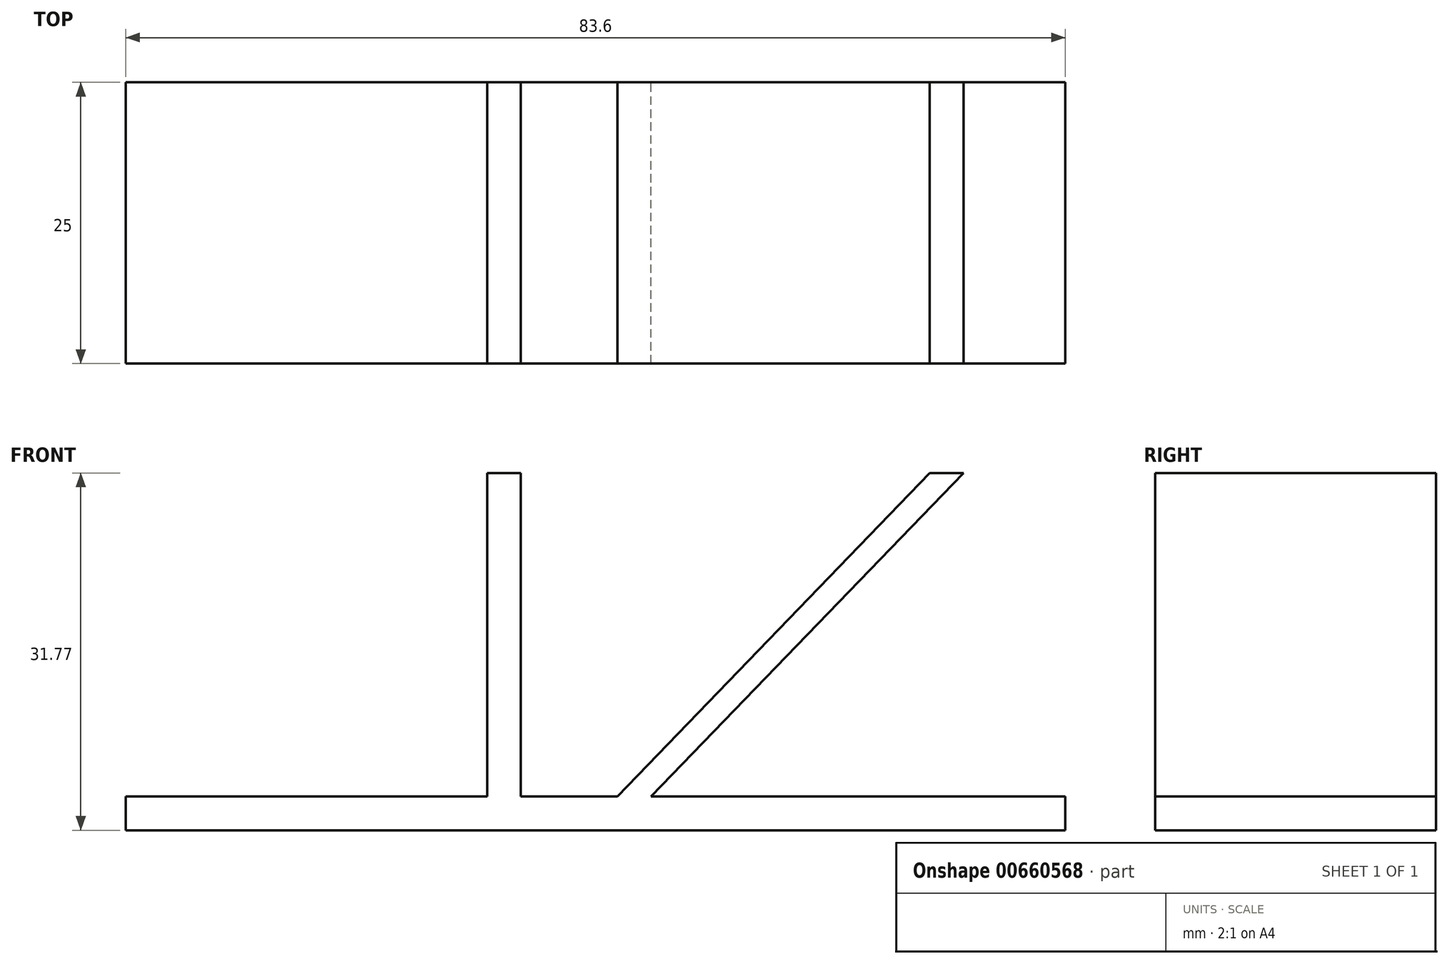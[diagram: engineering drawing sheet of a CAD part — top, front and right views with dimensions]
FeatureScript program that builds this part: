
annotation { "Feature Type Name" : "Feature", "Feature Type Description" : "" }
export const myFeature = defineFeature(function(context is Context, id is Id, definition is map)
    precondition{}
    {
        {
            var Q0;
            Q0=qCreatedBy(makeId("Front.planeOp"),FACE);
            var sketch = newSketch(context, id + "F0", { "sketchPlane" : qUnion([Q0])});
            skLineSegment(sketch, "E0", {"start": v(0, 0) * mm, "end": v(27.79, 28.77) * mm});
            skLineSegment(sketch, "E1", {"start": v(27.79, 28.77) * mm, "end": v(30.79, 28.77) * mm});
            skLineSegment(sketch, "E2", {"start": v(30.79, 28.77) * mm, "end": v(3, 0) * mm});
            skLineSegment(sketch, "E3", {"start": v(3, 0) * mm, "end": v(39.85, 0) * mm});
            skLineSegment(sketch, "E4", {"start": v(39.85, 0) * mm, "end": v(39.85, -3) * mm});
            skLineSegment(sketch, "E5", {"start": v(39.85, -3) * mm, "end": v(-43.75, -3) * mm});
            skLineSegment(sketch, "E6", {"start": v(-43.75, -3) * mm, "end": v(-43.75, 0) * mm});
            skLineSegment(sketch, "E7", {"start": v(-43.75, 0) * mm, "end": v(-11.6, 0) * mm});
            skLineSegment(sketch, "E8", {"start": v(-11.6, 0) * mm, "end": v(-11.6, 28.77) * mm});
            skLineSegment(sketch, "E9", {"start": v(-11.6, 28.77) * mm, "end": v(-8.6, 28.77) * mm});
            skLineSegment(sketch, "E10", {"start": v(-8.6, 28.77) * mm, "end": v(-8.6, 0) * mm});
            skLineSegment(sketch, "E11", {"start": v(-8.6, 0) * mm, "end": v(0, 0) * mm});
            skSolve(sketch);
        }
        {
            var Q0;
            Q0=makeQuery(id+"F0.imprint","IMPRINT",FACE,{"disambiguationData":[TD([[makeQuery(id+"F0.imprint","IMPRINT",EDGE,{"derivedFrom":sQuery(id+"F0.wireOp",EDGE,"E0")}),-1.0]])]});
            extrude(context, id + "F1", {"entities" : qUnion([Q0]), "depth" : 25 * mm, "offsetDistance" : 25 * mm});
        }
    });
